# Revit family: Roller_Shades-Lutron-Shade_Pocket
name_source: partatom
category: Specialty Equipment
revit_build: Autodesk Revit 2017 (Build: 20160225_1515(x64)
units: mm (PartAtom-declared; Revit-internal decimal feet)

## family parameters
Cut with Voids When Loaded = Yes
Host = Face
OmniClass Number = 23.30.60.14.21
OmniClass Title = Shades
Part Type = Normal
Room Calculation Point = No
Round Connector Dimension = Use Diameter
Shared = No

## types (1)
- Inside Mount
    Assembly Code = E2010320
    Cost = 0 $
    Default Elevation = 0' - 0"
    Description = Metal Roller Shade Pocket
    Instruction Sheet Link = http://www.lutron.com
    Light Gap = 0' - 0 3/4"
    Manufacturer = Lutron Electronics Co., Inc
    Manufacturer Fax Number = 610-282-1243
    Model = Manual Shade
    Product Documentation Link = http://www.lutron.com
    Product Name = Metal Roller Shade Pocket
    Product Page URL = http://www.lutron.com
    Series = Shade Pocket
    URL = http://www.lutron.com
    Version = 2017 - v1.0a
    Video Link = https://www.youtube.com
    Warranty URL = http://www.lutron.com

## geometry (parser evidence)
native form markers: Sweep x2
no freeform markers — native parametric forms only
